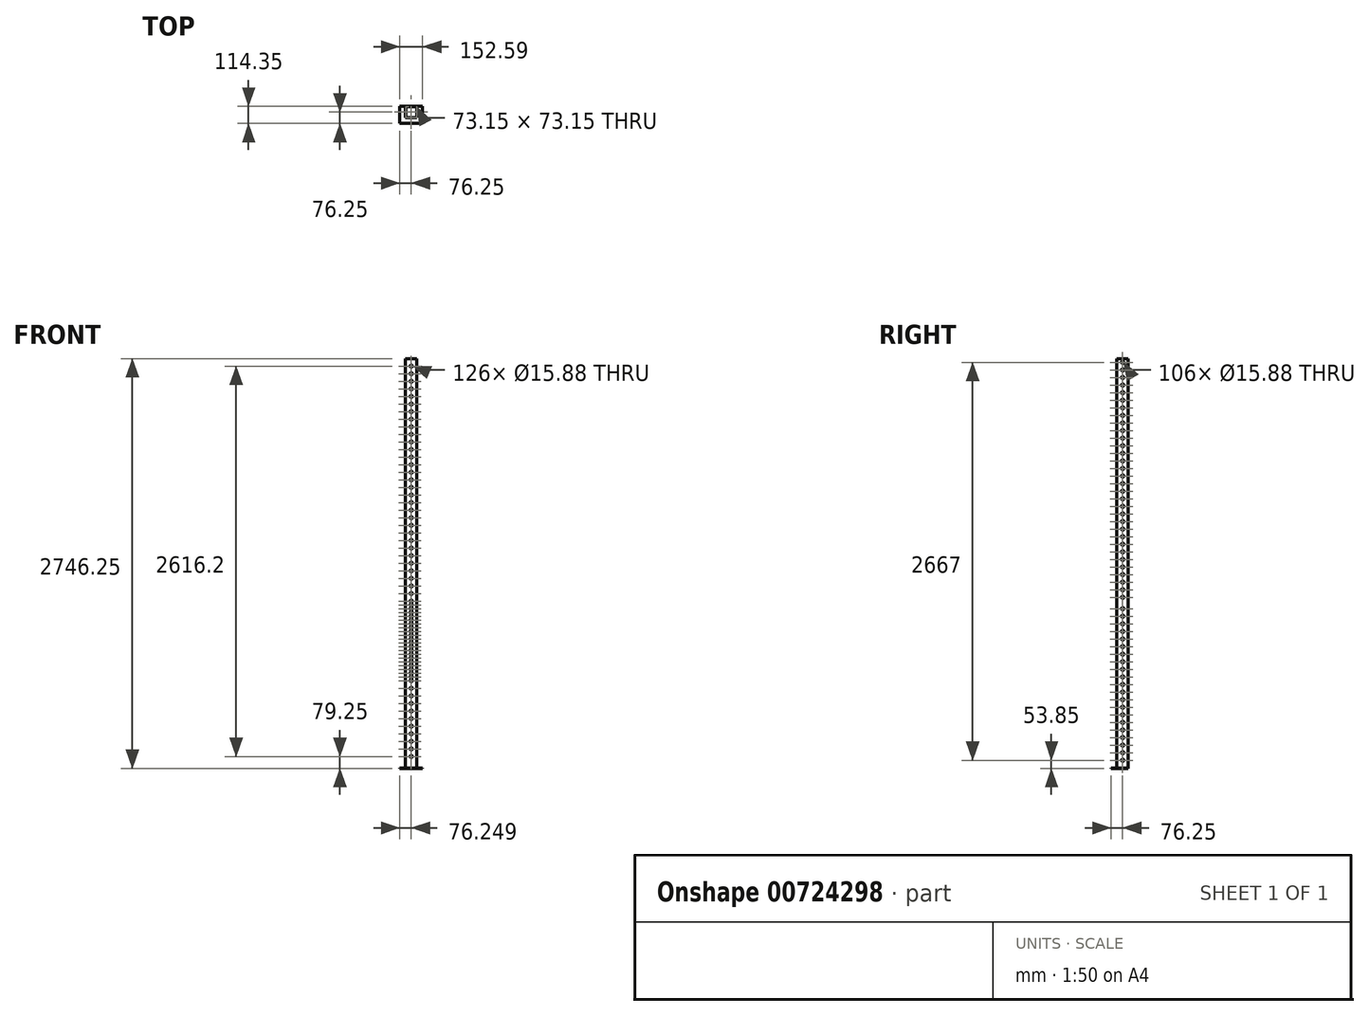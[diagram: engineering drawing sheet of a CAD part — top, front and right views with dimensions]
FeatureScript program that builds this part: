
annotation { "Feature Type Name" : "Feature", "Feature Type Description" : "" }
export const myFeature = defineFeature(function(context is Context, id is Id, definition is map)
    precondition{}
    {
        {
            var Q0;
            Q0=qCreatedBy(makeId("Top.planeOp"),FACE);
            var sketch = newSketch(context, id + "F0", { "sketchPlane" : qUnion([Q0])});
            skLineSegment(sketch, "E0.bottom", {"start": v(-38.1, -38.1) * mm, "end": v(38.1, -38.1) * mm});
            skLineSegment(sketch, "E0.top", {"start": v(-38.1, 38.1) * mm, "end": v(38.1, 38.1) * mm});
            skLineSegment(sketch, "E0.left", {"start": v(-38.1, -38.1) * mm, "end": v(-38.1, 38.1) * mm});
            skLineSegment(sketch, "E0.right", {"start": v(38.1, -38.1) * mm, "end": v(38.1, 38.1) * mm});
            skPoint(sketch, "E0.middle", {"position": v(0, 0) * mm});
            skLineSegment(sketch, "E1.bottom", {"start": v(-36.58, -36.58) * mm, "end": v(36.58, -36.58) * mm});
            skLineSegment(sketch, "E1.top", {"start": v(-36.58, 36.58) * mm, "end": v(36.58, 36.58) * mm});
            skLineSegment(sketch, "E1.left", {"start": v(-36.58, -36.58) * mm, "end": v(-36.58, 36.58) * mm});
            skLineSegment(sketch, "E1.right", {"start": v(36.58, -36.58) * mm, "end": v(36.58, 36.58) * mm});
            skLineSegment(sketch, "E2.bottom", {"start": v(-76.25, -76.25) * mm, "end": v(76.34, -76.25) * mm});
            skLineSegment(sketch, "E2.top", {"start": v(-76.25, 38.1) * mm, "end": v(76.34, 38.1) * mm});
            skLineSegment(sketch, "E2.left", {"start": v(-76.25, -76.25) * mm, "end": v(-76.25, 38.1) * mm});
            skLineSegment(sketch, "E2.right", {"start": v(76.34, -76.25) * mm, "end": v(76.34, 38.1) * mm});
            skSolve(sketch);
        }
        {
            var Q0;
            Q0=makeQuery(id+"F0.imprint","IMPRINT",FACE,{"disambiguationData":[TD([[makeQuery(id+"F0.imprint","IMPRINT",EDGE,{"derivedFrom":sQuery(id+"F0.wireOp",EDGE,"E0.bottom")}),-1.0]])]});
            extrude(context, id + "F1", {"entities" : qUnion([Q0]), "oppositeDirection" : true, "depth" : 3.05 * mm, "offsetDistance" : 25.4 * mm});
        }
        {
            var Q0;
            Q0=makeQuery(id+"F0.imprint","IMPRINT",FACE,{"disambiguationData":[TD([[makeQuery(id+"F0.imprint","IMPRINT",EDGE,{"derivedFrom":sQuery(id+"F0.wireOp",EDGE,"E0.bottom")}),1.0]])]});
            extrude(context, id + "F2", {"entities" : qUnion([Q0]), "operationType" : NewBodyOperationType.ADD, "depth" : 2743.2 * mm, "offsetDistance" : 25.4 * mm});
        }
        {
            var Q0;
            Q0=qCreatedBy(makeId("Front.planeOp"),FACE);
            cPlane(context, id + "F3", {"entities" : qUnion([Q0]), "cplaneType" : CPlaneType.OFFSET, "offset" : 76.2 * mm, "width" : 152.4 * mm, "height" : 152.4 * mm});
        }
        {
            var Q0;
            Q0=qCreatedBy(makeId("Right.planeOp"),FACE);
            cPlane(context, id + "F4", {"entities" : qUnion([Q0]), "cplaneType" : CPlaneType.OFFSET, "offset" : 76.2 * mm, "width" : 152.4 * mm, "height" : 152.4 * mm});
        }
        {
            var Q0;
            Q0=qCreatedBy(id+"F4.planeOp",FACE);
            var sketch = newSketch(context, id + "F5", { "sketchPlane" : qUnion([Q0])});
            skLineSegment(sketch, "E3.bottom", {"start": v(-38.1, 2743.2) * mm, "end": v(38.1, 2743.2) * mm});
            skLineSegment(sketch, "E3.top", {"start": v(-38.1, 0) * mm, "end": v(38.1, 0) * mm});
            skLineSegment(sketch, "E3.left", {"start": v(-38.1, 2743.2) * mm, "end": v(-38.1, 0) * mm});
            skLineSegment(sketch, "E3.right", {"start": v(38.1, 2743.2) * mm, "end": v(38.1, 0) * mm});
            skPoint(sketch, "E4", {"position": v(0, 50.8) * mm});
            skPoint(sketch, "E5.1.0.0", {"position": v(0, 101.6) * mm});
            skPoint(sketch, "E5.2.0.0", {"position": v(0, 152.4) * mm});
            skPoint(sketch, "E5.3.0.0", {"position": v(0, 203.2) * mm});
            skPoint(sketch, "E5.4.0.0", {"position": v(0, 254) * mm});
            skPoint(sketch, "E5.5.0.0", {"position": v(0, 304.8) * mm});
            skPoint(sketch, "E5.6.0.0", {"position": v(0, 355.6) * mm});
            skPoint(sketch, "E5.7.0.0", {"position": v(0, 406.4) * mm});
            skPoint(sketch, "E5.8.0.0", {"position": v(0, 457.2) * mm});
            skPoint(sketch, "E5.9.0.0", {"position": v(0, 508) * mm});
            skPoint(sketch, "E5.10.0.0", {"position": v(0, 558.8) * mm});
            skPoint(sketch, "E5.11.0.0", {"position": v(0, 609.6) * mm});
            skPoint(sketch, "E5.12.0.0", {"position": v(0, 660.4) * mm});
            skPoint(sketch, "E5.13.0.0", {"position": v(0, 711.2) * mm});
            skPoint(sketch, "E5.14.0.0", {"position": v(0, 762) * mm});
            skPoint(sketch, "E5.15.0.0", {"position": v(0, 812.8) * mm});
            skPoint(sketch, "E5.16.0.0", {"position": v(0, 863.6) * mm});
            skPoint(sketch, "E5.17.0.0", {"position": v(0, 914.4) * mm});
            skPoint(sketch, "E5.18.0.0", {"position": v(0, 965.2) * mm});
            skPoint(sketch, "E5.19.0.0", {"position": v(0, 1016) * mm});
            skPoint(sketch, "E5.20.0.0", {"position": v(0, 1066.8) * mm});
            skLineSegment(sketch, "E5.direction1", {"start": v(0, 50.8) * mm, "end": v(0, 101.6) * mm, "construction": true});
            skPoint(sketch, "E6", {"position": v(0, 1143) * mm});
            skPoint(sketch, "E7.1.0.0", {"position": v(0, 1193.8) * mm});
            skPoint(sketch, "E7.2.0.0", {"position": v(0, 1244.6) * mm});
            skPoint(sketch, "E7.3.0.0", {"position": v(0, 1295.4) * mm});
            skPoint(sketch, "E7.4.0.0", {"position": v(0, 1346.2) * mm});
            skPoint(sketch, "E7.5.0.0", {"position": v(0, 1397) * mm});
            skPoint(sketch, "E7.6.0.0", {"position": v(0, 1447.8) * mm});
            skPoint(sketch, "E7.7.0.0", {"position": v(0, 1498.6) * mm});
            skPoint(sketch, "E7.8.0.0", {"position": v(0, 1549.4) * mm});
            skPoint(sketch, "E7.9.0.0", {"position": v(0, 1600.2) * mm});
            skPoint(sketch, "E7.10.0.0", {"position": v(0, 1651) * mm});
            skPoint(sketch, "E7.11.0.0", {"position": v(0, 1701.8) * mm});
            skPoint(sketch, "E7.12.0.0", {"position": v(0, 1752.6) * mm});
            skPoint(sketch, "E7.13.0.0", {"position": v(0, 1803.4) * mm});
            skPoint(sketch, "E7.14.0.0", {"position": v(0, 1854.2) * mm});
            skPoint(sketch, "E7.15.0.0", {"position": v(0, 1905) * mm});
            skPoint(sketch, "E7.16.0.0", {"position": v(0, 1955.8) * mm});
            skPoint(sketch, "E7.17.0.0", {"position": v(0, 2006.6) * mm});
            skPoint(sketch, "E7.18.0.0", {"position": v(0, 2057.4) * mm});
            skPoint(sketch, "E7.19.0.0", {"position": v(0, 2108.2) * mm});
            skPoint(sketch, "E7.20.0.0", {"position": v(0, 2159) * mm});
            skPoint(sketch, "E7.21.0.0", {"position": v(0, 2209.8) * mm});
            skPoint(sketch, "E7.22.0.0", {"position": v(0, 2260.6) * mm});
            skPoint(sketch, "E7.23.0.0", {"position": v(0, 2311.4) * mm});
            skPoint(sketch, "E7.24.0.0", {"position": v(0, 2362.2) * mm});
            skPoint(sketch, "E7.25.0.0", {"position": v(0, 2413) * mm});
            skPoint(sketch, "E7.26.0.0", {"position": v(0, 2463.8) * mm});
            skPoint(sketch, "E7.27.0.0", {"position": v(0, 2514.6) * mm});
            skPoint(sketch, "E7.28.0.0", {"position": v(0, 2565.4) * mm});
            skPoint(sketch, "E7.29.0.0", {"position": v(0, 2616.2) * mm});
            skLineSegment(sketch, "E7.direction1", {"start": v(0, 1143) * mm, "end": v(0, 1193.8) * mm, "construction": true});
            skPoint(sketch, "E8.0.30.0", {"position": v(0, 2667) * mm});
            skPoint(sketch, "E8.0.31.0", {"position": v(0, 2717.8) * mm});
            skSolve(sketch);
        }
        {
            var Q0;
            Q0=qCreatedBy(id+"F3.planeOp",FACE);
            var sketch = newSketch(context, id + "F6", { "sketchPlane" : qUnion([Q0])});
            skLineSegment(sketch, "E9.bottom", {"start": v(-38.1, 2743.2) * mm, "end": v(38.1, 2743.2) * mm});
            skLineSegment(sketch, "E9.top", {"start": v(-38.1, 0) * mm, "end": v(38.1, 0) * mm});
            skLineSegment(sketch, "E9.left", {"start": v(-38.1, 2743.2) * mm, "end": v(-38.1, 0) * mm});
            skLineSegment(sketch, "E9.right", {"start": v(38.1, 2743.2) * mm, "end": v(38.1, 0) * mm});
            skPoint(sketch, "E10", {"position": v(0, 76.2) * mm});
            skPoint(sketch, "E11.1.0.0", {"position": v(0, 127) * mm});
            skPoint(sketch, "E11.2.0.0", {"position": v(0, 177.8) * mm});
            skPoint(sketch, "E11.3.0.0", {"position": v(0, 228.6) * mm});
            skPoint(sketch, "E11.4.0.0", {"position": v(0, 279.4) * mm});
            skPoint(sketch, "E11.5.0.0", {"position": v(0, 330.2) * mm});
            skPoint(sketch, "E11.6.0.0", {"position": v(0, 381) * mm});
            skPoint(sketch, "E11.7.0.0", {"position": v(0, 431.8) * mm});
            skPoint(sketch, "E11.8.0.0", {"position": v(0, 482.6) * mm});
            skPoint(sketch, "E11.9.0.0", {"position": v(0, 533.4) * mm});
            skLineSegment(sketch, "E11.direction1", {"start": v(0, 76.2) * mm, "end": v(0, 127) * mm, "construction": true});
            skPoint(sketch, "E12", {"position": v(0, 1168.4) * mm});
            skPoint(sketch, "E13.1.0.0", {"position": v(0, 1219.2) * mm});
            skPoint(sketch, "E13.2.0.0", {"position": v(0, 1270) * mm});
            skPoint(sketch, "E13.3.0.0", {"position": v(0, 1320.8) * mm});
            skPoint(sketch, "E13.4.0.0", {"position": v(0, 1371.6) * mm});
            skPoint(sketch, "E13.5.0.0", {"position": v(0, 1422.4) * mm});
            skPoint(sketch, "E13.6.0.0", {"position": v(0, 1473.2) * mm});
            skPoint(sketch, "E13.7.0.0", {"position": v(0, 1524) * mm});
            skPoint(sketch, "E13.8.0.0", {"position": v(0, 1574.8) * mm});
            skPoint(sketch, "E13.9.0.0", {"position": v(0, 1625.6) * mm});
            skPoint(sketch, "E13.10.0.0", {"position": v(0, 1676.4) * mm});
            skPoint(sketch, "E13.11.0.0", {"position": v(0, 1727.2) * mm});
            skPoint(sketch, "E13.12.0.0", {"position": v(0, 1778) * mm});
            skPoint(sketch, "E13.13.0.0", {"position": v(0, 1828.8) * mm});
            skPoint(sketch, "E13.14.0.0", {"position": v(0, 1879.6) * mm});
            skPoint(sketch, "E13.15.0.0", {"position": v(0, 1930.4) * mm});
            skPoint(sketch, "E13.16.0.0", {"position": v(0, 1981.2) * mm});
            skPoint(sketch, "E13.17.0.0", {"position": v(0, 2032) * mm});
            skPoint(sketch, "E13.18.0.0", {"position": v(0, 2082.8) * mm});
            skPoint(sketch, "E13.19.0.0", {"position": v(0, 2133.6) * mm});
            skPoint(sketch, "E13.20.0.0", {"position": v(0, 2184.4) * mm});
            skPoint(sketch, "E13.21.0.0", {"position": v(0, 2235.2) * mm});
            skPoint(sketch, "E13.22.0.0", {"position": v(0, 2286) * mm});
            skPoint(sketch, "E13.23.0.0", {"position": v(0, 2336.8) * mm});
            skPoint(sketch, "E13.24.0.0", {"position": v(0, 2387.6) * mm});
            skPoint(sketch, "E13.25.0.0", {"position": v(0, 2438.4) * mm});
            skPoint(sketch, "E13.26.0.0", {"position": v(0, 2489.2) * mm});
            skPoint(sketch, "E13.27.0.0", {"position": v(0, 2540) * mm});
            skPoint(sketch, "E13.28.0.0", {"position": v(0, 2590.8) * mm});
            skPoint(sketch, "E13.29.0.0", {"position": v(0, 2641.6) * mm});
            skLineSegment(sketch, "E13.direction1", {"start": v(0, 1168.4) * mm, "end": v(0, 1219.2) * mm, "construction": true});
            skPoint(sketch, "E14.0.30.0", {"position": v(0, 2692.4) * mm});
            skPoint(sketch, "E15.0.10.0", {"position": v(0, 584.2) * mm});
            skPoint(sketch, "E16.1.0.0", {"position": v(0, 609.6) * mm});
            skPoint(sketch, "E16.2.0.0", {"position": v(0, 635) * mm});
            skPoint(sketch, "E16.3.0.0", {"position": v(0, 660.4) * mm});
            skPoint(sketch, "E16.4.0.0", {"position": v(0, 685.8) * mm});
            skPoint(sketch, "E16.5.0.0", {"position": v(0, 711.2) * mm});
            skPoint(sketch, "E16.6.0.0", {"position": v(0, 736.6) * mm});
            skPoint(sketch, "E16.7.0.0", {"position": v(0, 762) * mm});
            skPoint(sketch, "E16.8.0.0", {"position": v(0, 787.4) * mm});
            skPoint(sketch, "E16.9.0.0", {"position": v(0, 812.8) * mm});
            skPoint(sketch, "E16.10.0.0", {"position": v(0, 838.2) * mm});
            skPoint(sketch, "E16.11.0.0", {"position": v(0, 863.6) * mm});
            skPoint(sketch, "E16.12.0.0", {"position": v(0, 889) * mm});
            skPoint(sketch, "E16.13.0.0", {"position": v(0, 914.4) * mm});
            skPoint(sketch, "E16.14.0.0", {"position": v(0, 939.8) * mm});
            skPoint(sketch, "E16.15.0.0", {"position": v(0, 965.2) * mm});
            skPoint(sketch, "E16.16.0.0", {"position": v(0, 990.6) * mm});
            skPoint(sketch, "E16.17.0.0", {"position": v(0, 1016) * mm});
            skPoint(sketch, "E16.18.0.0", {"position": v(0, 1041.4) * mm});
            skPoint(sketch, "E16.19.0.0", {"position": v(0, 1066.8) * mm});
            skPoint(sketch, "E16.20.0.0", {"position": v(0, 1092.2) * mm});
            skLineSegment(sketch, "E16.direction1", {"start": v(0, 584.2) * mm, "end": v(0, 609.6) * mm, "construction": true});
            skPoint(sketch, "E17.0.21.0", {"position": v(0, 1117.6) * mm});
            skSolve(sketch);
        }
        {
            var Q0;
            Q0=sQuery(id+"F6.wireOp",VERTEX,"E10");
            var Q1;
            Q1=sQuery(id+"F6.wireOp",VERTEX,"E11.1.0.0");
            var Q2;
            Q2=sQuery(id+"F6.wireOp",VERTEX,"E11.2.0.0");
            var Q3;
            Q3=sQuery(id+"F6.wireOp",VERTEX,"E11.3.0.0");
            var Q4;
            Q4=sQuery(id+"F6.wireOp",VERTEX,"E11.4.0.0");
            var Q5;
            Q5=sQuery(id+"F6.wireOp",VERTEX,"E11.5.0.0");
            var Q6;
            Q6=sQuery(id+"F6.wireOp",VERTEX,"E11.6.0.0");
            var Q7;
            Q7=sQuery(id+"F6.wireOp",VERTEX,"E11.7.0.0");
            var Q8;
            Q8=sQuery(id+"F6.wireOp",VERTEX,"E11.8.0.0");
            var Q9;
            Q9=sQuery(id+"F6.wireOp",VERTEX,"E11.9.0.0");
            var Q10;
            Q10=sQuery(id+"F6.wireOp",VERTEX,"E15.0.10.0");
            var Q11;
            Q11=sQuery(id+"F6.wireOp",VERTEX,"E16.1.0.0");
            var Q12;
            Q12=sQuery(id+"F6.wireOp",VERTEX,"E16.2.0.0");
            var Q13;
            Q13=sQuery(id+"F6.wireOp",VERTEX,"E16.3.0.0");
            var Q14;
            Q14=sQuery(id+"F6.wireOp",VERTEX,"E16.4.0.0");
            var Q15;
            Q15=sQuery(id+"F6.wireOp",VERTEX,"E16.5.0.0");
            var Q16;
            Q16=sQuery(id+"F6.wireOp",VERTEX,"E16.6.0.0");
            var Q17;
            Q17=sQuery(id+"F6.wireOp",VERTEX,"E16.7.0.0");
            var Q18;
            Q18=sQuery(id+"F6.wireOp",VERTEX,"E16.8.0.0");
            var Q19;
            Q19=sQuery(id+"F6.wireOp",VERTEX,"E16.9.0.0");
            var Q20;
            Q20=sQuery(id+"F6.wireOp",VERTEX,"E16.10.0.0");
            var Q21;
            Q21=sQuery(id+"F6.wireOp",VERTEX,"E16.11.0.0");
            var Q22;
            Q22=sQuery(id+"F6.wireOp",VERTEX,"E16.12.0.0");
            var Q23;
            Q23=sQuery(id+"F6.wireOp",VERTEX,"E16.13.0.0");
            var Q24;
            Q24=sQuery(id+"F6.wireOp",VERTEX,"E16.14.0.0");
            var Q25;
            Q25=sQuery(id+"F6.wireOp",VERTEX,"E16.15.0.0");
            var Q26;
            Q26=sQuery(id+"F6.wireOp",VERTEX,"E16.16.0.0");
            var Q27;
            Q27=sQuery(id+"F6.wireOp",VERTEX,"E16.17.0.0");
            var Q28;
            Q28=sQuery(id+"F6.wireOp",VERTEX,"E16.18.0.0");
            var Q29;
            Q29=sQuery(id+"F6.wireOp",VERTEX,"E16.19.0.0");
            var Q30;
            Q30=sQuery(id+"F6.wireOp",VERTEX,"E16.20.0.0");
            var Q31;
            Q31=sQuery(id+"F6.wireOp",VERTEX,"E17.0.21.0");
            var Q32;
            Q32=sQuery(id+"F6.wireOp",VERTEX,"E12");
            var Q33;
            Q33=sQuery(id+"F6.wireOp",VERTEX,"E13.1.0.0");
            var Q34;
            Q34=sQuery(id+"F6.wireOp",VERTEX,"E13.2.0.0");
            var Q35;
            Q35=sQuery(id+"F6.wireOp",VERTEX,"E13.3.0.0");
            var Q36;
            Q36=sQuery(id+"F6.wireOp",VERTEX,"E13.4.0.0");
            var Q37;
            Q37=sQuery(id+"F6.wireOp",VERTEX,"E13.5.0.0");
            var Q38;
            Q38=sQuery(id+"F6.wireOp",VERTEX,"E13.6.0.0");
            var Q39;
            Q39=sQuery(id+"F6.wireOp",VERTEX,"E13.7.0.0");
            var Q40;
            Q40=sQuery(id+"F6.wireOp",VERTEX,"E13.8.0.0");
            var Q41;
            Q41=sQuery(id+"F6.wireOp",VERTEX,"E13.9.0.0");
            var Q42;
            Q42=sQuery(id+"F6.wireOp",VERTEX,"E13.10.0.0");
            var Q43;
            Q43=sQuery(id+"F6.wireOp",VERTEX,"E13.11.0.0");
            var Q44;
            Q44=sQuery(id+"F6.wireOp",VERTEX,"E13.12.0.0");
            var Q45;
            Q45=sQuery(id+"F6.wireOp",VERTEX,"E13.13.0.0");
            var Q46;
            Q46=sQuery(id+"F6.wireOp",VERTEX,"E13.14.0.0");
            var Q47;
            Q47=sQuery(id+"F6.wireOp",VERTEX,"E13.15.0.0");
            var Q48;
            Q48=sQuery(id+"F6.wireOp",VERTEX,"E13.16.0.0");
            var Q49;
            Q49=sQuery(id+"F6.wireOp",VERTEX,"E13.17.0.0");
            var Q50;
            Q50=sQuery(id+"F6.wireOp",VERTEX,"E13.18.0.0");
            var Q51;
            Q51=sQuery(id+"F6.wireOp",VERTEX,"E13.19.0.0");
            var Q52;
            Q52=sQuery(id+"F6.wireOp",VERTEX,"E13.20.0.0");
            var Q53;
            Q53=sQuery(id+"F6.wireOp",VERTEX,"E13.21.0.0");
            var Q54;
            Q54=sQuery(id+"F6.wireOp",VERTEX,"E13.22.0.0");
            var Q55;
            Q55=sQuery(id+"F6.wireOp",VERTEX,"E13.23.0.0");
            var Q56;
            Q56=sQuery(id+"F6.wireOp",VERTEX,"E13.24.0.0");
            var Q57;
            Q57=sQuery(id+"F6.wireOp",VERTEX,"E13.25.0.0");
            var Q58;
            Q58=sQuery(id+"F6.wireOp",VERTEX,"E13.26.0.0");
            var Q59;
            Q59=sQuery(id+"F6.wireOp",VERTEX,"E13.27.0.0");
            var Q60;
            Q60=sQuery(id+"F6.wireOp",VERTEX,"E13.28.0.0");
            var Q61;
            Q61=sQuery(id+"F6.wireOp",VERTEX,"E13.29.0.0");
            var Q62;
            Q62=sQuery(id+"F6.wireOp",VERTEX,"E14.0.30.0");
            var Q63;
            {var subQ0=sQuery(id+"F0.wireOp",EDGE,"E0.right");var subQ1=sQuery(id+"F0.wireOp",EDGE,"E0.left");var subQ2=sQuery(id+"F0.wireOp",EDGE,"E0.top");var subQ3=sQuery(id+"F0.wireOp",EDGE,"E0.bottom");Q63=makeQuery(id+"F2.boolean.opBoolean","MERGE",BODY,{"derivedFrom":[makeQuery(id+"F1.opExtrude","SWEPT_BODY",BODY,{"disambiguationData":[OSD([subQ3,subQ2,subQ1,subQ0,sQuery(id+"F0.wireOp",EDGE,"E2.bottom"),sQuery(id+"F0.wireOp",EDGE,"E2.top"),sQuery(id+"F0.wireOp",EDGE,"E2.left"),sQuery(id+"F0.wireOp",EDGE,"E2.right")])]}),makeQuery(id+"F2.opExtrude","SWEPT_BODY",BODY,{"disambiguationData":[OSD([subQ3,subQ2,subQ1,subQ0,sQuery(id+"F0.wireOp",EDGE,"E1.bottom"),sQuery(id+"F0.wireOp",EDGE,"E1.top"),sQuery(id+"F0.wireOp",EDGE,"E1.left"),sQuery(id+"F0.wireOp",EDGE,"E1.right")])]})]});}
            hole(context, id + "F7", {"style" : HoleStyle.SIMPLE, "endStyle" : HoleEndStyle.THROUGH, "holeDiameter" : 15.88 * mm, "majorDiameter" : 6.35 * mm, "isTappedThrough" : true, "tappedDepth" : 12.7 * mm, "tapClearance" : 3, "locations" : qUnion([Q0, Q1, Q2, Q3, Q4, Q5, Q6, Q7, Q8, Q9, Q10, Q11, Q12, Q13, Q14, Q15, Q16, Q17, Q18, Q19, Q20, Q21, Q22, Q23, Q24, Q25, Q26, Q27, Q28, Q29, Q30, Q31, Q32, Q33, Q34, Q35, Q36, Q37, Q38, Q39, Q40, Q41, Q42, Q43, Q44, Q45, Q46, Q47, Q48, Q49, Q50, Q51, Q52, Q53, Q54, Q55, Q56, Q57, Q58, Q59, Q60, Q61, Q62]), "scope" : qUnion([Q63])});
        }
        {
            var Q0;
            Q0=sQuery(id+"F5.wireOp",VERTEX,"E4");
            var Q1;
            Q1=sQuery(id+"F5.wireOp",VERTEX,"E5.1.0.0");
            var Q2;
            Q2=sQuery(id+"F5.wireOp",VERTEX,"E5.2.0.0");
            var Q3;
            Q3=sQuery(id+"F5.wireOp",VERTEX,"E5.3.0.0");
            var Q4;
            Q4=sQuery(id+"F5.wireOp",VERTEX,"E5.4.0.0");
            var Q5;
            Q5=sQuery(id+"F5.wireOp",VERTEX,"E5.5.0.0");
            var Q6;
            Q6=sQuery(id+"F5.wireOp",VERTEX,"E5.6.0.0");
            var Q7;
            Q7=sQuery(id+"F5.wireOp",VERTEX,"E5.7.0.0");
            var Q8;
            Q8=sQuery(id+"F5.wireOp",VERTEX,"E5.8.0.0");
            var Q9;
            Q9=sQuery(id+"F5.wireOp",VERTEX,"E5.9.0.0");
            var Q10;
            Q10=sQuery(id+"F5.wireOp",VERTEX,"E5.10.0.0");
            var Q11;
            Q11=sQuery(id+"F5.wireOp",VERTEX,"E5.11.0.0");
            var Q12;
            Q12=sQuery(id+"F5.wireOp",VERTEX,"E5.12.0.0");
            var Q13;
            Q13=sQuery(id+"F5.wireOp",VERTEX,"E5.13.0.0");
            var Q14;
            Q14=sQuery(id+"F5.wireOp",VERTEX,"E5.14.0.0");
            var Q15;
            Q15=sQuery(id+"F5.wireOp",VERTEX,"E5.15.0.0");
            var Q16;
            Q16=sQuery(id+"F5.wireOp",VERTEX,"E5.16.0.0");
            var Q17;
            Q17=sQuery(id+"F5.wireOp",VERTEX,"E5.17.0.0");
            var Q18;
            Q18=sQuery(id+"F5.wireOp",VERTEX,"E5.18.0.0");
            var Q19;
            Q19=sQuery(id+"F5.wireOp",VERTEX,"E5.19.0.0");
            var Q20;
            Q20=sQuery(id+"F5.wireOp",VERTEX,"E5.20.0.0");
            var Q21;
            Q21=sQuery(id+"F5.wireOp",VERTEX,"E6");
            var Q22;
            Q22=sQuery(id+"F5.wireOp",VERTEX,"E7.1.0.0");
            var Q23;
            Q23=sQuery(id+"F5.wireOp",VERTEX,"E7.2.0.0");
            var Q24;
            Q24=sQuery(id+"F5.wireOp",VERTEX,"E7.3.0.0");
            var Q25;
            Q25=sQuery(id+"F5.wireOp",VERTEX,"E7.4.0.0");
            var Q26;
            Q26=sQuery(id+"F5.wireOp",VERTEX,"E7.5.0.0");
            var Q27;
            Q27=sQuery(id+"F5.wireOp",VERTEX,"E7.6.0.0");
            var Q28;
            Q28=sQuery(id+"F5.wireOp",VERTEX,"E7.7.0.0");
            var Q29;
            Q29=sQuery(id+"F5.wireOp",VERTEX,"E7.8.0.0");
            var Q30;
            Q30=sQuery(id+"F5.wireOp",VERTEX,"E7.9.0.0");
            var Q31;
            Q31=sQuery(id+"F5.wireOp",VERTEX,"E7.10.0.0");
            var Q32;
            Q32=sQuery(id+"F5.wireOp",VERTEX,"E7.11.0.0");
            var Q33;
            Q33=sQuery(id+"F5.wireOp",VERTEX,"E7.12.0.0");
            var Q34;
            Q34=sQuery(id+"F5.wireOp",VERTEX,"E7.13.0.0");
            var Q35;
            Q35=sQuery(id+"F5.wireOp",VERTEX,"E7.14.0.0");
            var Q36;
            Q36=sQuery(id+"F5.wireOp",VERTEX,"E7.15.0.0");
            var Q37;
            Q37=sQuery(id+"F5.wireOp",VERTEX,"E7.16.0.0");
            var Q38;
            Q38=sQuery(id+"F5.wireOp",VERTEX,"E7.17.0.0");
            var Q39;
            Q39=sQuery(id+"F5.wireOp",VERTEX,"E7.18.0.0");
            var Q40;
            Q40=sQuery(id+"F5.wireOp",VERTEX,"E7.19.0.0");
            var Q41;
            Q41=sQuery(id+"F5.wireOp",VERTEX,"E7.20.0.0");
            var Q42;
            Q42=sQuery(id+"F5.wireOp",VERTEX,"E7.21.0.0");
            var Q43;
            Q43=sQuery(id+"F5.wireOp",VERTEX,"E7.22.0.0");
            var Q44;
            Q44=sQuery(id+"F5.wireOp",VERTEX,"E7.23.0.0");
            var Q45;
            Q45=sQuery(id+"F5.wireOp",VERTEX,"E7.24.0.0");
            var Q46;
            Q46=sQuery(id+"F5.wireOp",VERTEX,"E7.25.0.0");
            var Q47;
            Q47=sQuery(id+"F5.wireOp",VERTEX,"E7.26.0.0");
            var Q48;
            Q48=sQuery(id+"F5.wireOp",VERTEX,"E7.27.0.0");
            var Q49;
            Q49=sQuery(id+"F5.wireOp",VERTEX,"E7.28.0.0");
            var Q50;
            Q50=sQuery(id+"F5.wireOp",VERTEX,"E7.29.0.0");
            var Q51;
            Q51=sQuery(id+"F5.wireOp",VERTEX,"E8.0.30.0");
            var Q52;
            Q52=sQuery(id+"F5.wireOp",VERTEX,"E8.0.31.0");
            var Q53;
            {var subQ0=sQuery(id+"F0.wireOp",EDGE,"E0.right");var subQ1=sQuery(id+"F0.wireOp",EDGE,"E0.left");var subQ2=sQuery(id+"F0.wireOp",EDGE,"E0.top");var subQ3=sQuery(id+"F0.wireOp",EDGE,"E0.bottom");Q53=makeQuery(id+"F2.boolean.opBoolean","MERGE",BODY,{"derivedFrom":[makeQuery(id+"F1.opExtrude","SWEPT_BODY",BODY,{"disambiguationData":[OSD([subQ3,subQ2,subQ1,subQ0,sQuery(id+"F0.wireOp",EDGE,"E2.bottom"),sQuery(id+"F0.wireOp",EDGE,"E2.top"),sQuery(id+"F0.wireOp",EDGE,"E2.left"),sQuery(id+"F0.wireOp",EDGE,"E2.right")])]}),makeQuery(id+"F2.opExtrude","SWEPT_BODY",BODY,{"disambiguationData":[OSD([subQ3,subQ2,subQ1,subQ0,sQuery(id+"F0.wireOp",EDGE,"E1.bottom"),sQuery(id+"F0.wireOp",EDGE,"E1.top"),sQuery(id+"F0.wireOp",EDGE,"E1.left"),sQuery(id+"F0.wireOp",EDGE,"E1.right")])]})]});}
            hole(context, id + "F8", {"style" : HoleStyle.SIMPLE, "endStyle" : HoleEndStyle.THROUGH, "holeDiameter" : 15.88 * mm, "majorDiameter" : 6.35 * mm, "isTappedThrough" : true, "tappedDepth" : 12.7 * mm, "tapClearance" : 3, "locations" : qUnion([Q0, Q1, Q2, Q3, Q4, Q5, Q6, Q7, Q8, Q9, Q10, Q11, Q12, Q13, Q14, Q15, Q16, Q17, Q18, Q19, Q20, Q21, Q22, Q23, Q24, Q25, Q26, Q27, Q28, Q29, Q30, Q31, Q32, Q33, Q34, Q35, Q36, Q37, Q38, Q39, Q40, Q41, Q42, Q43, Q44, Q45, Q46, Q47, Q48, Q49, Q50, Q51, Q52]), "scope" : qUnion([Q53])});
        }
    });
